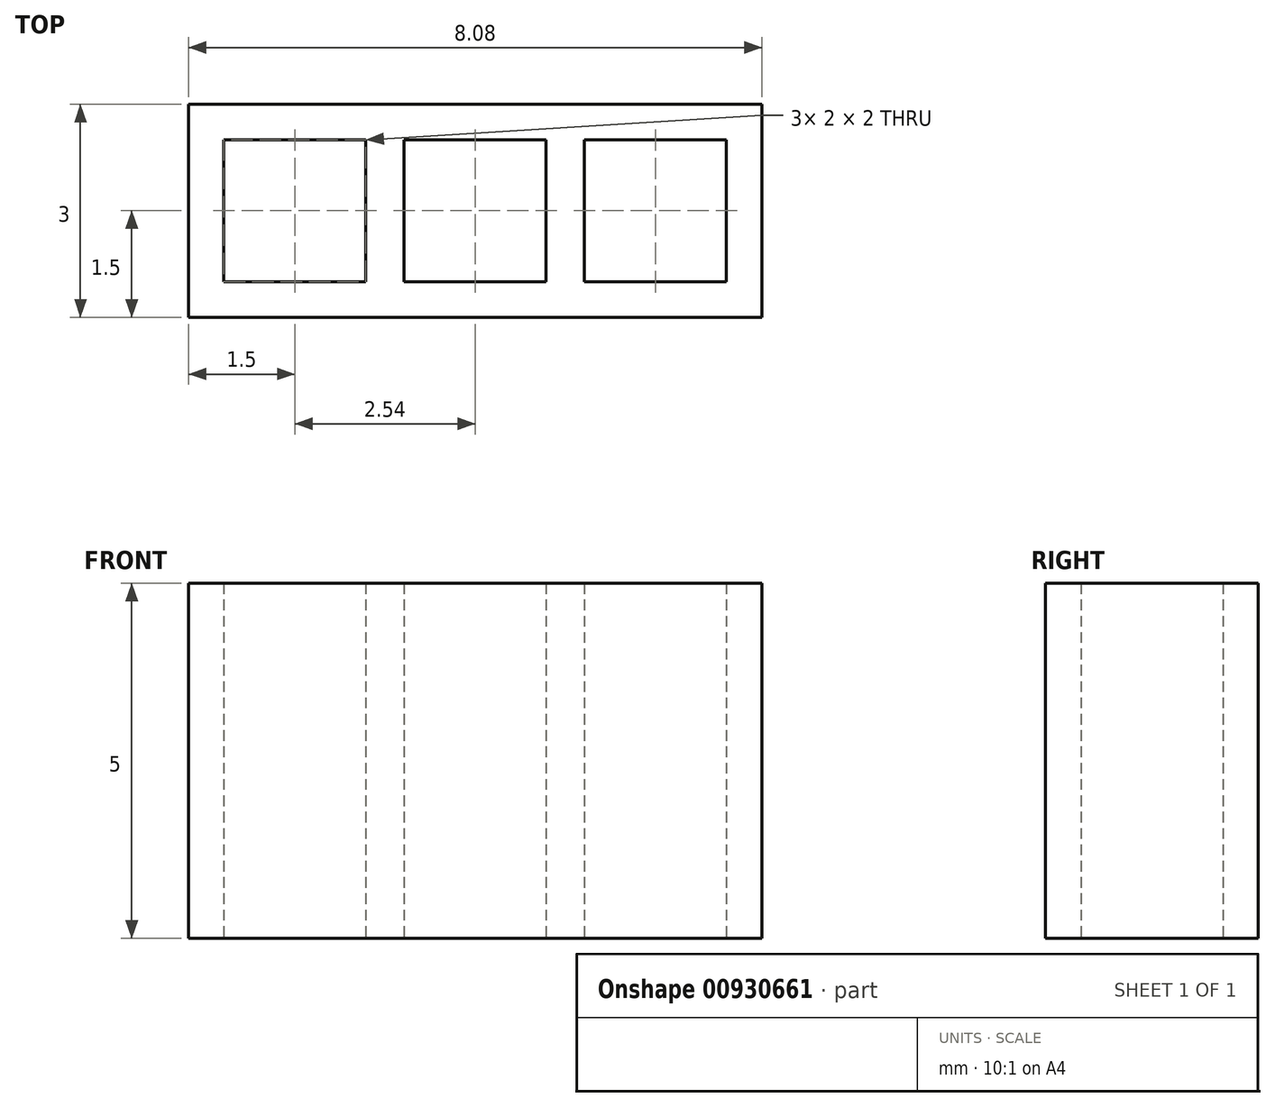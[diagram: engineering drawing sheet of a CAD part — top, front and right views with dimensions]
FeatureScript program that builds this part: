
annotation { "Feature Type Name" : "Feature", "Feature Type Description" : "" }
export const myFeature = defineFeature(function(context is Context, id is Id, definition is map)
    precondition{}
    {
        {
            var Q0;
            Q0=qCreatedBy(makeId("Top.planeOp"),FACE);
            var sketch = newSketch(context, id + "F0", { "sketchPlane" : qUnion([Q0])});
            skLineSegment(sketch, "E0.bottom", {"start": v(0, 0) * mm, "end": v(8.08, 0) * mm});
            skLineSegment(sketch, "E0.top", {"start": v(0, 3) * mm, "end": v(8.08, 3) * mm});
            skLineSegment(sketch, "E0.left", {"start": v(0, 0) * mm, "end": v(0, 3) * mm});
            skLineSegment(sketch, "E0.right", {"start": v(8.08, 0) * mm, "end": v(8.08, 3) * mm});
            skLineSegment(sketch, "E1.bottom", {"start": v(0.5, 2.5) * mm, "end": v(2.5, 2.5) * mm});
            skLineSegment(sketch, "E1.top", {"start": v(0.5, 0.5) * mm, "end": v(2.5, 0.5) * mm});
            skLineSegment(sketch, "E1.left", {"start": v(0.5, 2.5) * mm, "end": v(0.5, 0.5) * mm});
            skLineSegment(sketch, "E1.right", {"start": v(2.5, 2.5) * mm, "end": v(2.5, 0.5) * mm});
            skLineSegment(sketch, "E2.bottom", {"start": v(3.04, 2.5) * mm, "end": v(5.04, 2.5) * mm});
            skLineSegment(sketch, "E2.top", {"start": v(3.04, 0.5) * mm, "end": v(5.04, 0.5) * mm});
            skLineSegment(sketch, "E2.left", {"start": v(3.04, 2.5) * mm, "end": v(3.04, 0.5) * mm});
            skLineSegment(sketch, "E2.right", {"start": v(5.04, 2.5) * mm, "end": v(5.04, 0.5) * mm});
            skLineSegment(sketch, "E3.bottom", {"start": v(5.58, 2.5) * mm, "end": v(7.58, 2.5) * mm});
            skLineSegment(sketch, "E3.top", {"start": v(5.58, 0.5) * mm, "end": v(7.58, 0.5) * mm});
            skLineSegment(sketch, "E3.left", {"start": v(5.58, 2.5) * mm, "end": v(5.58, 0.5) * mm});
            skLineSegment(sketch, "E3.right", {"start": v(7.58, 2.5) * mm, "end": v(7.58, 0.5) * mm});
            skSolve(sketch);
        }
        {
            var Q0;
            Q0=qSketchRegion(id+"F0",true);
            extrude(context, id + "F1", {"entities" : qUnion([Q0]), "depth" : 5 * mm, "offsetDistance" : 25 * mm});
        }
    });
